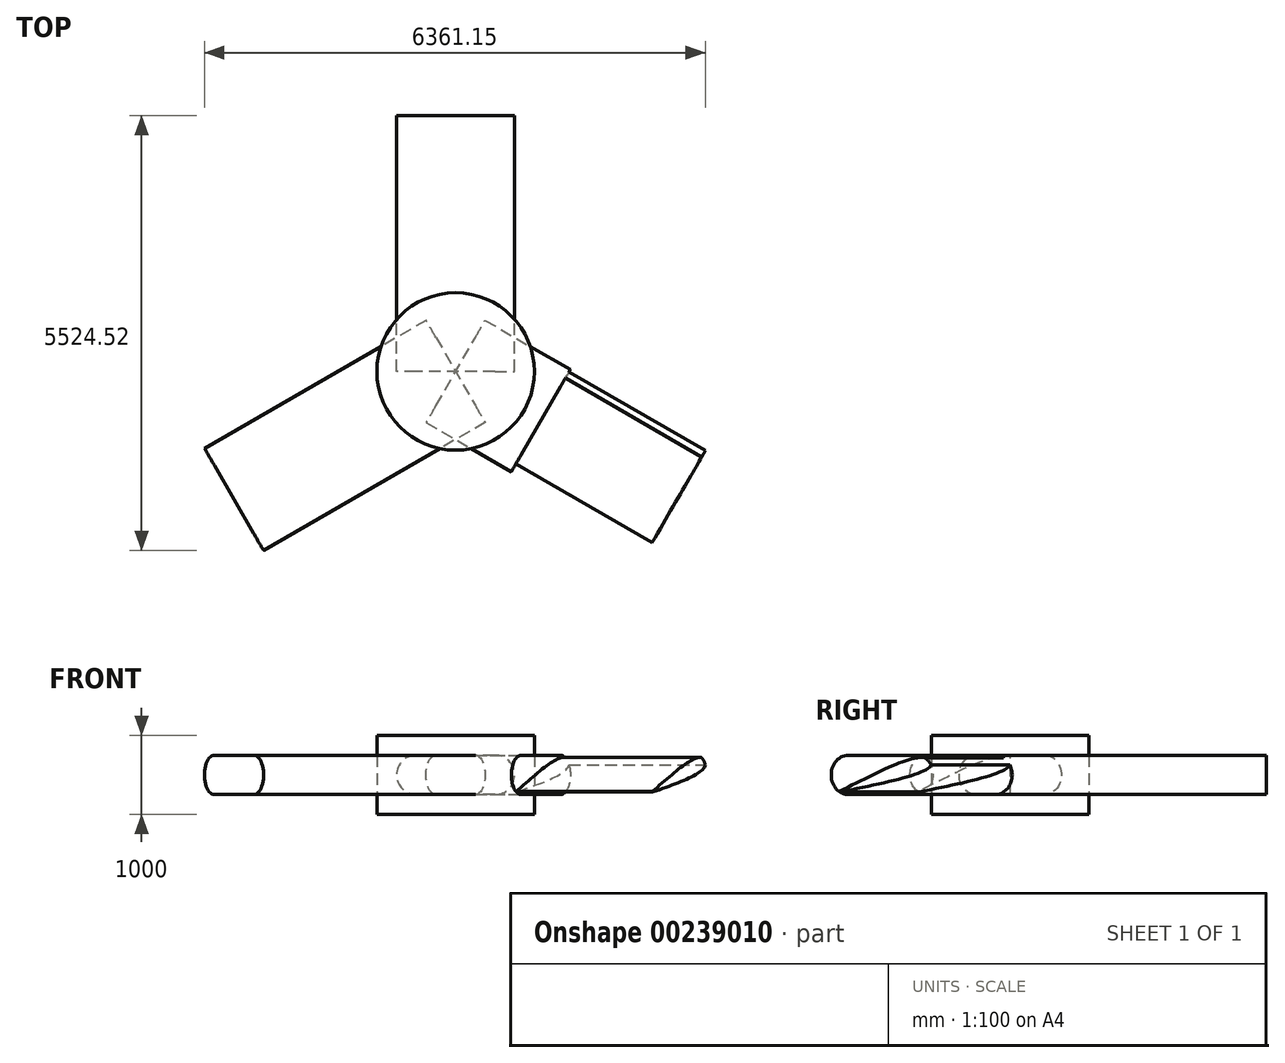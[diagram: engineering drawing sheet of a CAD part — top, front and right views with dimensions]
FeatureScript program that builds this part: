
annotation { "Feature Type Name" : "Feature", "Feature Type Description" : "" }
export const myFeature = defineFeature(function(context is Context, id is Id, definition is map)
    precondition{}
    {
        {
            var Q0;
            Q0=qCreatedBy(makeId("Top.planeOp"),FACE);
            var sketch = newSketch(context, id + "F0", { "sketchPlane" : qUnion([Q0])});
            skCircle(sketch, "E0", {"center": v(0, 0) * mm, "radius": 3250 * mm});
            skCircle(sketch, "E1", {"center": v(0, 0) * mm, "radius": 1000 * mm});
            skLineSegment(sketch, "E2", {"start": v(0, 0) * mm, "end": v(0, 3250) * mm});
            skLineSegment(sketch, "E3.1.0", {"start": v(0, 0) * mm, "end": v(-2814.58, -1625) * mm});
            skLineSegment(sketch, "E3.2.0", {"start": v(0, 0) * mm, "end": v(2814.58, -1625) * mm});
            skSolve(sketch);
        }
        {
            var Q0;
            {var subQ0=sQuery(id+"F0.wireOp",EDGE,"E3.1.0");var subQ1=sQuery(id+"F0.wireOp",EDGE,"E1");var subQ2=makeQuery(id+"F0.imprint","INTERSECT",VERTEX,{"derivedFrom":[subQ1,subQ0]});Q0=makeQuery(id+"F0.imprint","IMPRINT",FACE,{"disambiguationData":[TD([[makeQuery(id+"F0.imprint","IMPRINT",EDGE,{"disambiguationData":[TD([[subQ2,1.0]])],"derivedFrom":subQ1}),1.0]])]});}
            var Q1;
            {var subQ0=sQuery(id+"F0.wireOp",EDGE,"E2");var subQ1=sQuery(id+"F0.wireOp",EDGE,"E1");var subQ2=makeQuery(id+"F0.imprint","INTERSECT",VERTEX,{"derivedFrom":[subQ1,subQ0]});Q1=makeQuery(id+"F0.imprint","IMPRINT",FACE,{"disambiguationData":[TD([[makeQuery(id+"F0.imprint","IMPRINT",EDGE,{"disambiguationData":[TD([[subQ2,1.0]])],"derivedFrom":subQ1}),1.0]])]});}
            var Q2;
            {var subQ0=sQuery(id+"F0.wireOp",EDGE,"E3.1.0");var subQ1=sQuery(id+"F0.wireOp",EDGE,"E1");var subQ2=makeQuery(id+"F0.imprint","INTERSECT",VERTEX,{"derivedFrom":[subQ1,subQ0]});Q2=makeQuery(id+"F0.imprint","IMPRINT",FACE,{"disambiguationData":[TD([[makeQuery(id+"F0.imprint","IMPRINT",EDGE,{"disambiguationData":[TD([[subQ2,-1.0]])],"derivedFrom":subQ1}),1.0]])]});}
            extrude(context, id + "F1", {"entities" : qUnion([Q0, Q1, Q2]), "endBound" : BoundingType.SYMMETRIC, "depth" : 1000 * mm});
        }
        {
            var Q0;
            Q0=qCreatedBy(makeId("Front.planeOp"),FACE);
            var sketch = newSketch(context, id + "F2", { "sketchPlane" : qUnion([Q0])});
            skLineSegment(sketch, "E4.bottom", {"start": v(500, 250) * mm, "end": v(-500, 250) * mm});
            skLineSegment(sketch, "E4.top", {"start": v(500, -250) * mm, "end": v(-500, -250) * mm});
            skLineSegment(sketch, "E4.left", {"start": v(500, 250) * mm, "end": v(500, -250) * mm});
            skLineSegment(sketch, "E4.right", {"start": v(-500, 250) * mm, "end": v(-500, -250) * mm});
            skPoint(sketch, "E4.middle", {"position": v(0, 0) * mm});
            skArc(sketch, "E5", {"start": v(500, 250) * mm, "mid": v(750, 0) * mm, "end": v(500, -250) * mm});
            skArc(sketch, "E6", {"start": v(-500, -250) * mm, "mid": v(-750, 0) * mm, "end": v(-500, 250) * mm});
            skSolve(sketch);
        }
        {
            var Q0;
            Q0 = qSketchRegion(id + "F2", true);
            var Q1;
            Q1=sQuery(id+"F0.wireOp",EDGE,"E2");
            sweep(context, id + "F3", {"profiles" : qUnion([Q0]), "path" : qUnion([Q1])});
        }
        {
            var Q0;
            Q0=makeQuery(id+"F3.opSweep","SWEPT_BODY",BODY,{"disambiguationData":[OSD([sQuery(id+"F0.wireOp",EDGE,"E2"),sQuery(id+"F2.wireOp",EDGE,"E4.bottom"),sQuery(id+"F2.wireOp",EDGE,"E4.top"),sQuery(id+"F2.wireOp",EDGE,"E5"),sQuery(id+"F2.wireOp",EDGE,"E6")])]});
            var Q1;
            Q1=makeQuery(id+"F1.opExtrude","SWEPT_FACE",FACE,{"disambiguationData":[OSD([sQuery(id+"F0.wireOp",EDGE,"E1")])]});
            circularPattern(context, id + "F4", {"entities" : qUnion([Q0]), "axis" : qUnion([Q1]), "angle" : 360 * degree, "instanceCount" : 3, "equalSpace" : true});
        }
        {
            var Q0;
            Q0=makeQuery(id+"F4.opPattern","COPY",FACE,{"derivedFrom":makeQuery(id+"F3.opSweep","CAP_FACE",FACE,{"disambiguationData":[OSD([sQuery(id+"F0.wireOp",VERTEX,"E2.end"),sQuery(id+"F2.wireOp",EDGE,"E4.bottom"),sQuery(id+"F2.wireOp",EDGE,"E4.top"),sQuery(id+"F2.wireOp",EDGE,"E5"),sQuery(id+"F2.wireOp",EDGE,"E6")])],"isStart":false}),"instanceName":"1"});
            var sketch = newSketch(context, id + "F5", { "sketchPlane" : qUnion([Q0])});
            skPoint(sketch, "E7", {"position": v(-622.83, -217.74) * mm});
            skPoint(sketch, "E8", {"position": v(622.83, 217.74) * mm});
            skPoint(sketch, "E9", {"position": v(713.97, 129.3) * mm});
            skFitSpline(sketch, "E10", {"points": [v(-622.83, -217.74) * mm, v(713.97, 129.3) * mm, v(622.83, 217.74) * mm, v(-633.73, -211.22) * mm], "startDerivative": vector(4416.39, 770.18) * mm, "endDerivative": vector(-3692.22, -1574.88) * mm});
            skSolve(sketch);
        }
        {
            var Q0;
            {var subQ1=sQuery(id+"F0.wireOp",VERTEX,"E2.end");var subQ6=makeQuery(id+"F4.opPattern","COPY",EDGE,{"derivedFrom":makeQuery(id+"F3.opSweep","CAP_EDGE",EDGE,{"disambiguationData":[OSD([subQ1,sQuery(id+"F2.wireOp",EDGE,"E4.bottom")])],"isStart":false}),"instanceName":"1"});Q0=makeQuery(id+"F5.imprint","IMPRINT",FACE,{"disambiguationData":[TD([[makeQuery(id+"F5.imprint","IMPRINT",EDGE,{"derivedFrom":subQ6}),1.0]])]});}
            var Q1;
            {var subQ1=sQuery(id+"F0.wireOp",VERTEX,"E2.end");var subQ6=makeQuery(id+"F4.opPattern","COPY",EDGE,{"derivedFrom":makeQuery(id+"F3.opSweep","CAP_EDGE",EDGE,{"disambiguationData":[OSD([subQ1,sQuery(id+"F2.wireOp",EDGE,"E4.top")])],"isStart":false}),"instanceName":"1"});Q1=makeQuery(id+"F5.imprint","IMPRINT",FACE,{"disambiguationData":[TD([[makeQuery(id+"F5.imprint","IMPRINT",EDGE,{"derivedFrom":subQ6}),1.0]])]});}
            extrude(context, id + "F6", {"entities" : qUnion([Q0, Q1]), "operationType" : NewBodyOperationType.REMOVE, "oppositeDirection" : true, "depth" : 2000 * mm});
        }
    });
